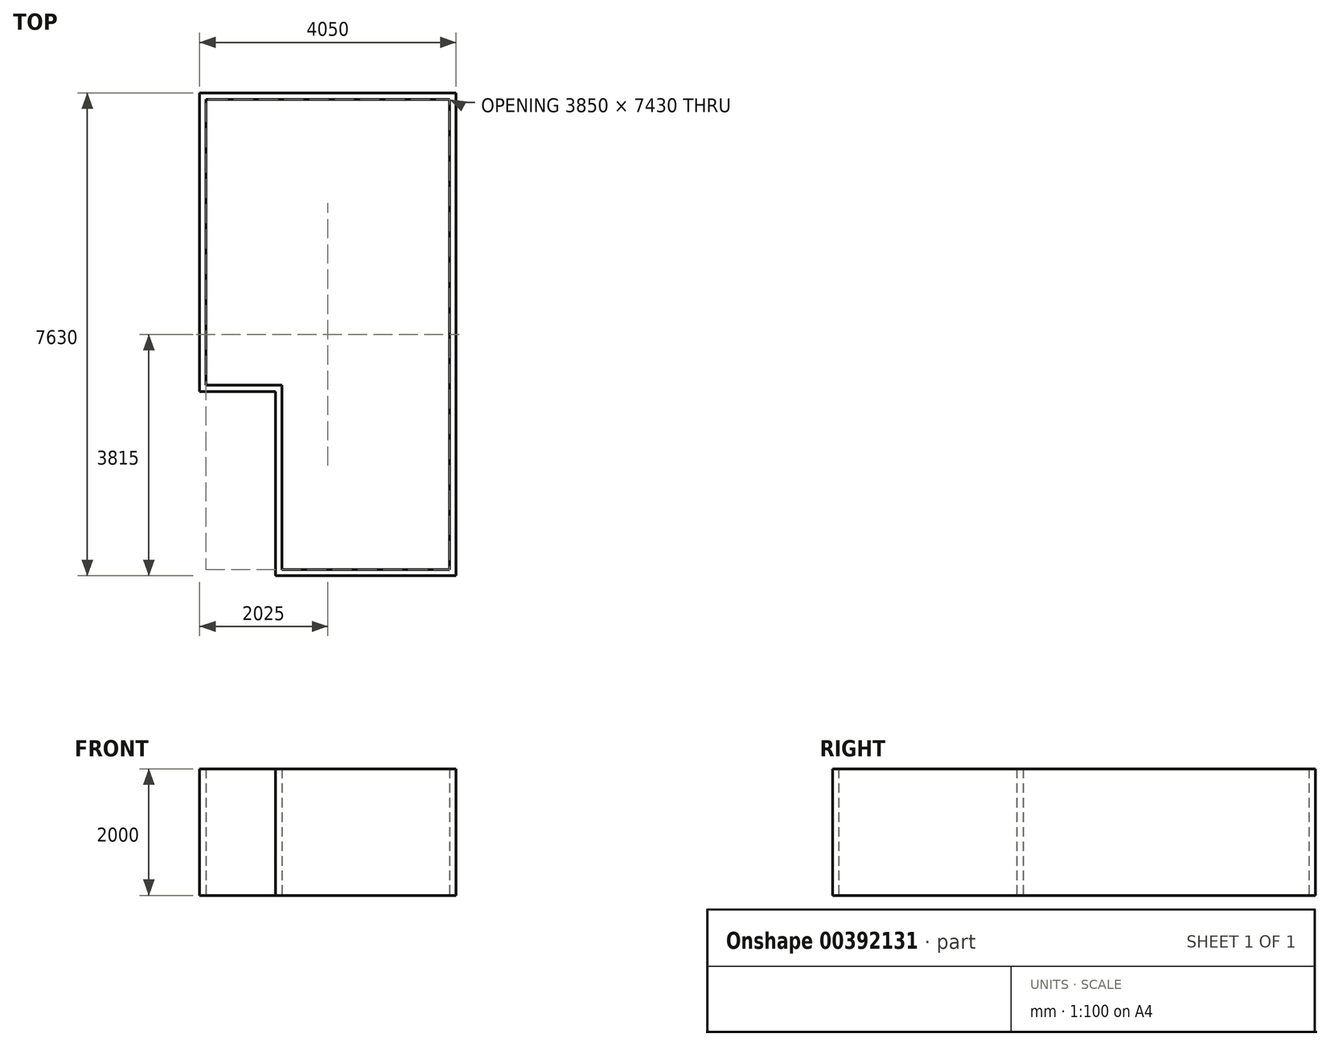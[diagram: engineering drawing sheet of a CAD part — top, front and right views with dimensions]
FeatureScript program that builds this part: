
annotation { "Feature Type Name" : "Feature", "Feature Type Description" : "" }
export const myFeature = defineFeature(function(context is Context, id is Id, definition is map)
    precondition{}
    {
        {
            var Q0;
            Q0=qCreatedBy(makeId("Top.planeOp"),FACE);
            var sketch = newSketch(context, id + "F0", { "sketchPlane" : qUnion([Q0])});
            skLineSegment(sketch, "E0", {"start": v(1425, 0) * mm, "end": v(1425, 7630) * mm});
            skLineSegment(sketch, "E1", {"start": v(0, 0) * mm, "end": v(1425, 0) * mm});
            skLineSegment(sketch, "E2", {"start": v(0, 0) * mm, "end": v(-1425, 0) * mm});
            skLineSegment(sketch, "E3", {"start": v(-1425, 0) * mm, "end": v(-1425, 2910) * mm});
            skLineSegment(sketch, "E4", {"start": v(-1425, 2910) * mm, "end": v(-2625, 2910) * mm});
            skLineSegment(sketch, "E5", {"start": v(-2625, 2910) * mm, "end": v(-2625, 7630) * mm});
            skLineSegment(sketch, "E6", {"start": v(-2625, 7630) * mm, "end": v(1425, 7630) * mm});
            skLineSegment(sketch, "E7.0", {"start": v(-1325, 3010) * mm, "end": v(-2525, 3010) * mm});
            skLineSegment(sketch, "E7.1", {"start": v(-1325, 100) * mm, "end": v(-1325, 3010) * mm});
            skLineSegment(sketch, "E7.2", {"start": v(-2525, 7530) * mm, "end": v(1325, 7530) * mm});
            skLineSegment(sketch, "E7.3", {"start": v(1325, 100) * mm, "end": v(1325, 7530) * mm});
            skLineSegment(sketch, "E7.4", {"start": v(0, 100) * mm, "end": v(1325, 100) * mm});
            skLineSegment(sketch, "E7.5", {"start": v(-2525, 3010) * mm, "end": v(-2525, 7530) * mm});
            skLineSegment(sketch, "E7.6", {"start": v(0, 100) * mm, "end": v(-1325, 100) * mm});
            skSolve(sketch);
        }
        {
            var Q0;
            Q0 = qSketchRegion(id + "F0", true);
            extrude(context, id + "F1", {"entities" : qUnion([Q0]), "depth" : 2000 * mm});
        }
    });
